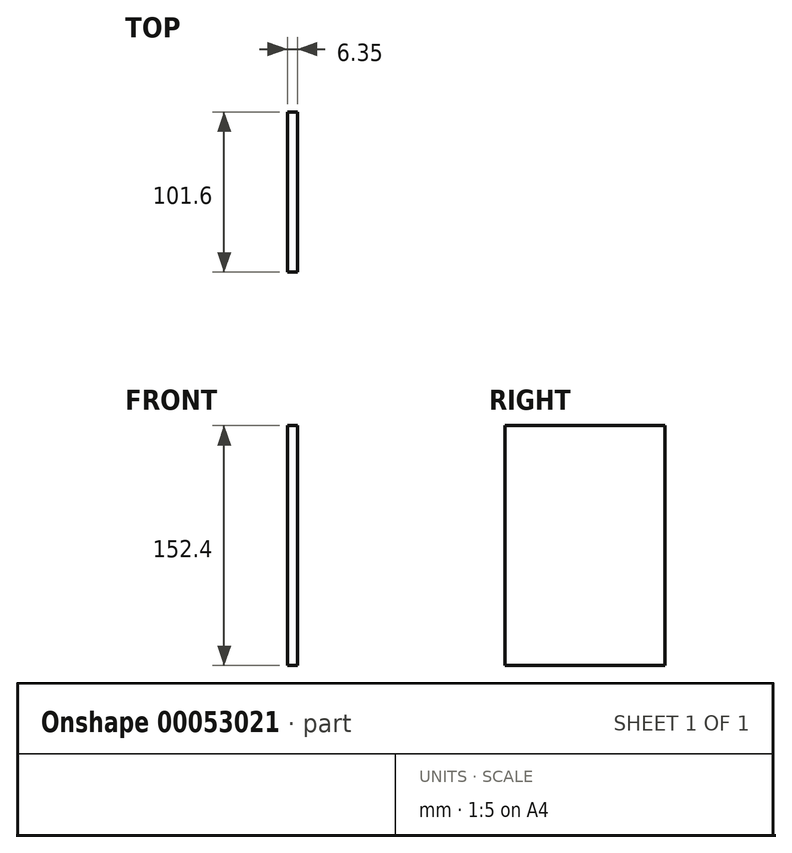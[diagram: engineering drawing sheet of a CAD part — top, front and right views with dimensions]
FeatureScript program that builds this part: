
annotation { "Feature Type Name" : "Feature", "Feature Type Description" : "" }
export const myFeature = defineFeature(function(context is Context, id is Id, definition is map)
    precondition{}
    {
        {
            var Q0;
            Q0=qCreatedBy(makeId("Right.planeOp"),FACE);
            var sketch = newSketch(context, id + "F0", { "sketchPlane" : qUnion([Q0])});
            skLineSegment(sketch, "E0.bottom", {"start": v(0, 0) * mm, "end": v(-101.6, 0) * mm});
            skLineSegment(sketch, "E0.top", {"start": v(0, 152.4) * mm, "end": v(-101.6, 152.4) * mm});
            skLineSegment(sketch, "E0.left", {"start": v(0, 0) * mm, "end": v(0, 152.4) * mm});
            skLineSegment(sketch, "E0.right", {"start": v(-101.6, 0) * mm, "end": v(-101.6, 152.4) * mm});
            skSolve(sketch);
        }
        {
            var Q0;
            Q0 = qSketchRegion(id + "F0", true);
            extrude(context, id + "F1", {"entities" : qUnion([Q0]), "depth" : 6.35 * mm});
        }
    });
